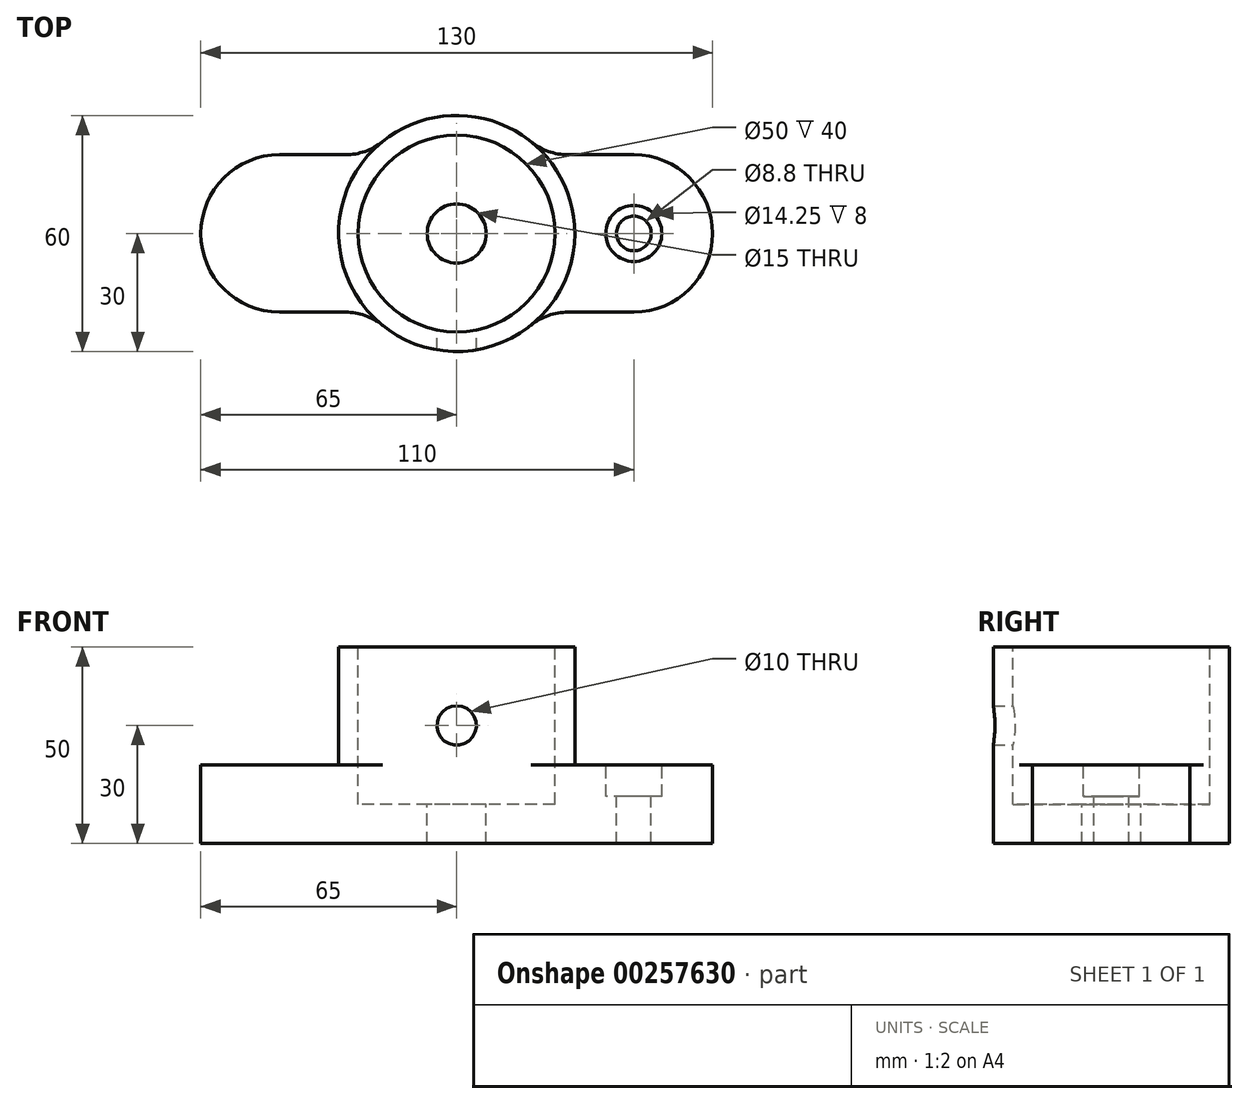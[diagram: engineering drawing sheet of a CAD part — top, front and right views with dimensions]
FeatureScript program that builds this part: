
annotation { "Feature Type Name" : "Feature", "Feature Type Description" : "" }
export const myFeature = defineFeature(function(context is Context, id is Id, definition is map)
    precondition{}
    {
        {
            var Q0;
            Q0=qCreatedBy(makeId("Top.planeOp"),FACE);
            var sketch = newSketch(context, id + "F0", { "sketchPlane" : qUnion([Q0])});
            skLineSegment(sketch, "E0.bottom", {"start": v(45, -20) * mm, "end": v(-45, -20) * mm});
            skLineSegment(sketch, "E0.top", {"start": v(45, 20) * mm, "end": v(-45, 20) * mm});
            skLineSegment(sketch, "E0.left", {"start": v(45, -20) * mm, "end": v(45, 20) * mm, "construction": true});
            skLineSegment(sketch, "E0.right", {"start": v(-45, -20) * mm, "end": v(-45, 20) * mm, "construction": true});
            skPoint(sketch, "E0.middle", {"position": v(0, 0) * mm});
            skArc(sketch, "E1", {"start": v(-45, 20) * mm, "mid": v(-65, 0) * mm, "end": v(-45, -20) * mm});
            skArc(sketch, "E2", {"start": v(45, -20) * mm, "mid": v(65, 0) * mm, "end": v(45, 20) * mm});
            skSolve(sketch);
        }
        {
            var Q0;
            Q0 = qSketchRegion(id + "F0", true);
            extrude(context, id + "F1", {"entities" : qUnion([Q0]), "depth" : 20 * mm});
        }
        {
            var Q0;
            Q0=qCreatedBy(makeId("Top.planeOp"),FACE);
            var sketch = newSketch(context, id + "F2", { "sketchPlane" : qUnion([Q0])});
            skCircle(sketch, "E3", {"center": v(0, 0) * mm, "radius": 30 * mm});
            skSolve(sketch);
        }
        {
            var Q0;
            Q0 = qSketchRegion(id + "F2", true);
            extrude(context, id + "F3", {"entities" : qUnion([Q0]), "operationType" : NewBodyOperationType.ADD, "depth" : 50 * mm});
        }
        {
            var Q0;
            Q0=makeQuery(id+"F3.opExtrude","CAP_FACE",FACE,{"disambiguationData":[OSD([sQuery(id+"F2.wireOp",EDGE,"E3")])],"isStart":false});
            var sketch = newSketch(context, id + "F4", { "sketchPlane" : qUnion([Q0])});
            skCircle(sketch, "E4", {"center": v(0, 0) * mm, "radius": 25 * mm});
            skSolve(sketch);
        }
        {
            var Q0;
            Q0 = qSketchRegion(id + "F4", true);
            extrude(context, id + "F5", {"entities" : qUnion([Q0]), "operationType" : NewBodyOperationType.REMOVE, "oppositeDirection" : true, "depth" : 40 * mm});
        }
        {
            var Q0;
            {var subQ0=sQuery(id+"F0.wireOp",EDGE,"E0.bottom");var subQ1=sQuery(id+"F0.wireOp",EDGE,"E0.top");var subQ2=sQuery(id+"F0.wireOp",EDGE,"E2");Q0=makeQuery(id+"F3.boolean.opBoolean","SPLIT",FACE,{"disambiguationData":[TD([makeQuery(id+"F1.opExtrude","SWEPT_FACE",FACE,{"disambiguationData":[OSD([subQ2])]})])],"derivedFrom":makeQuery(id+"F1.opExtrude","CAP_FACE",FACE,{"disambiguationData":[OSD([subQ0,subQ1,sQuery(id+"F0.wireOp",EDGE,"E1"),subQ2])],"isStart":false})});}
            var sketch = newSketch(context, id + "F6", { "sketchPlane" : qUnion([Q0])});
            skPoint(sketch, "E5", {"position": v(45, 0) * mm});
            skSolve(sketch);
        }
        {
            var Q0;
            Q0=sQuery(id+"F6.wireOp",VERTEX,"E5");
            var Q1;
            Q1=makeQuery(id+"F1.opExtrude","SWEPT_BODY",BODY,{"disambiguationData":[OSD([sQuery(id+"F0.wireOp",EDGE,"E0.bottom"),sQuery(id+"F0.wireOp",EDGE,"E0.top"),sQuery(id+"F0.wireOp",EDGE,"E1"),sQuery(id+"F0.wireOp",EDGE,"E2")])]});
            hole(context, id + "F7", {"style" : HoleStyle.C_BORE, "endStyle" : HoleEndStyle.THROUGH, "standardTappedOrClearance" : lookupTablePath({ "standard" : "ISO", "fit" : "Normal", "size" : "M8", "type" : "Clearance" }), "standardBlindInLast" : lookupTablePath({ "fit" : "Standard", "standard" : "ISO", "size" : "M8", "type" : "Clearance" }), "holeDiameter" : 8.8 * mm, "cBoreDiameter" : 14.25 * mm, "cBoreDepth" : 8 * mm, "tappedDepth" : 12 * mm, "tapClearance" : 3, "startFromSketch" : true, "locations" : qUnion([Q0]), "scope" : qUnion([Q1])});
        }
        {
            var Q0;
            Q0=qCreatedBy(makeId("Front.planeOp"),FACE);
            var sketch = newSketch(context, id + "F8", { "sketchPlane" : qUnion([Q0])});
            skCircle(sketch, "E6", {"center": v(0, 30) * mm, "radius": 5 * mm});
            skSolve(sketch);
        }
        {
            var Q0;
            Q0 = qSketchRegion(id + "F8", true);
            extrude(context, id + "F9", {"entities" : qUnion([Q0]), "operationType" : NewBodyOperationType.REMOVE, "endBound" : BoundingType.THROUGH_ALL, "depth" : 25 * mm});
        }
        {
            var Q0;
            Q0=makeQuery(id+"F5.boolean.opBoolean","COPY",FACE,{"derivedFrom":makeQuery(id+"F5.opExtrude","CAP_FACE",FACE,{"disambiguationData":[OSD([sQuery(id+"F4.wireOp",EDGE,"E4")])],"isStart":false})});
            var sketch = newSketch(context, id + "F10", { "sketchPlane" : qUnion([Q0])});
            skCircle(sketch, "E7", {"center": v(0, 0) * mm, "radius": 7.5 * mm});
            skSolve(sketch);
        }
        {
            var Q0;
            Q0 = qSketchRegion(id + "F10", true);
            extrude(context, id + "F11", {"entities" : qUnion([Q0]), "operationType" : NewBodyOperationType.REMOVE, "endBound" : BoundingType.UP_TO_NEXT, "oppositeDirection" : true, "depth" : 25 * mm});
        }
        {
            var Q0;
            Q0=makeQuery(id+"F3.boolean.opBoolean","INTERSECT",EDGE,{"disambiguationData":[OD(0.0)],"derivedFrom":[makeQuery(id+"F1.opExtrude","SWEPT_FACE",FACE,{"disambiguationData":[OSD([sQuery(id+"F0.wireOp",EDGE,"E0.bottom")])]}),makeQuery(id+"F3.opExtrude","SWEPT_FACE",FACE,{"disambiguationData":[OSD([sQuery(id+"F2.wireOp",EDGE,"E3")])]})]});
            var Q1;
            Q1=makeQuery(id+"F3.boolean.opBoolean","INTERSECT",EDGE,{"disambiguationData":[OD(1.0)],"derivedFrom":[makeQuery(id+"F1.opExtrude","SWEPT_FACE",FACE,{"disambiguationData":[OSD([sQuery(id+"F0.wireOp",EDGE,"E0.bottom")])]}),makeQuery(id+"F3.opExtrude","SWEPT_FACE",FACE,{"disambiguationData":[OSD([sQuery(id+"F2.wireOp",EDGE,"E3")])]})]});
            var Q2;
            Q2=makeQuery(id+"F3.boolean.opBoolean","INTERSECT",EDGE,{"disambiguationData":[OD(0.0)],"derivedFrom":[makeQuery(id+"F1.opExtrude","SWEPT_FACE",FACE,{"disambiguationData":[OSD([sQuery(id+"F0.wireOp",EDGE,"E0.top")])]}),makeQuery(id+"F3.opExtrude","SWEPT_FACE",FACE,{"disambiguationData":[OSD([sQuery(id+"F2.wireOp",EDGE,"E3")])]})]});
            var Q3;
            Q3=makeQuery(id+"F3.boolean.opBoolean","INTERSECT",EDGE,{"disambiguationData":[OD(1.0)],"derivedFrom":[makeQuery(id+"F1.opExtrude","SWEPT_FACE",FACE,{"disambiguationData":[OSD([sQuery(id+"F0.wireOp",EDGE,"E0.top")])]}),makeQuery(id+"F3.opExtrude","SWEPT_FACE",FACE,{"disambiguationData":[OSD([sQuery(id+"F2.wireOp",EDGE,"E3")])]})]});
            fillet(context, id + "F12", {"entities" : qUnion([Q0, Q1, Q2, Q3]), "radius" : 15 * mm, "tangentPropagation" : true, "allowEdgeOverflow" : false});
        }
    });
